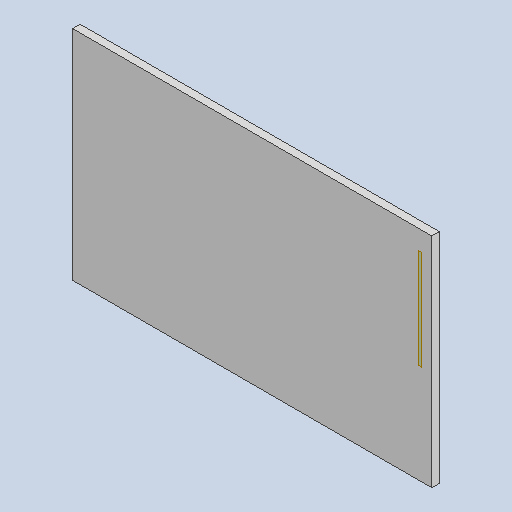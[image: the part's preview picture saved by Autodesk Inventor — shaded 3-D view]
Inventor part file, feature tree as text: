
AUTODESK INVENTOR PART (.ipt)
format: ipt  version: 2023.2 (Build 272271000, 271)  size: 78,848 bytes
history: native  units: mm
features: plane x1, extrude x1, sketch x1
ambient origin geometry x8: Origin, YZ Plane, XZ Plane, XY Plane, X Axis, Y Axis, Z Axis, Center Point
bodies: Solid1 (feature_tree)
feature tree (3):
  plane  "Work Plane1"
  extrude  "Extrusion1"  [1 undecoded]
  sketch  "Sketch1"  dims[d0=50.0mm d1=0.0mm]
note: 1 required parameter value undecoded (feature->parameter linkage not recoverable at this tier; creation-order binding heuristic only, values carry confidence <= 0.55)
